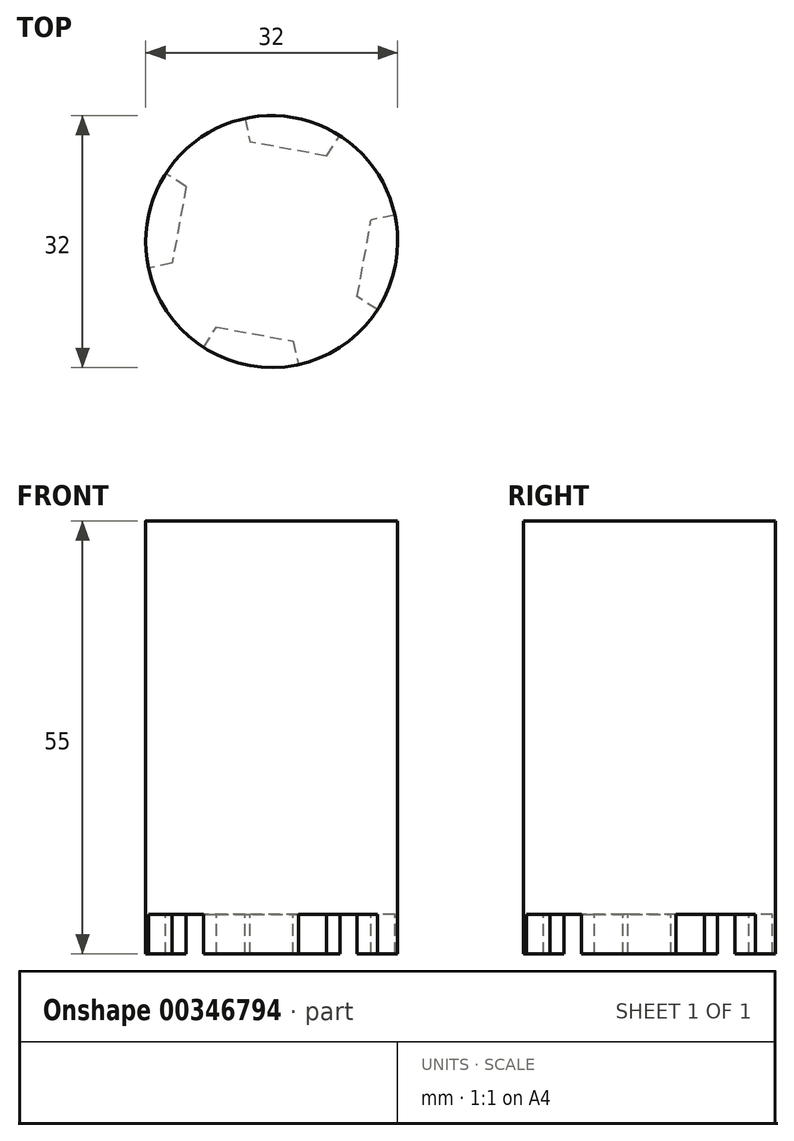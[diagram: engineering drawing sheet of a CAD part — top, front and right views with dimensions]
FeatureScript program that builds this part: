
annotation { "Feature Type Name" : "Feature", "Feature Type Description" : "" }
export const myFeature = defineFeature(function(context is Context, id is Id, definition is map)
    precondition{}
    {
        {
            var Q0;
            Q0=qCreatedBy(makeId("Top.planeOp"),FACE);
            var sketch = newSketch(context, id + "F0", { "sketchPlane" : qUnion([Q0])});
            skCircle(sketch, "E0", {"center": v(41.4, -34.31) * mm, "radius": 16 * mm});
            skSolve(sketch);
        }
        {
            var Q0;
            Q0 = qSketchRegion(id + "F0", true);
            extrude(context, id + "F1", {"entities" : qUnion([Q0]), "depth" : 50 * mm});
        }
        {
            var Q0;
            Q0=makeQuery(id+"F1.opExtrude","CAP_FACE",FACE,{"disambiguationData":[OSD([sQuery(id+"F0.wireOp",EDGE,"E0")])],"isStart":true});
            var sketch = newSketch(context, id + "F2", { "sketchPlane" : qUnion([Q0])});
            skCircle(sketch, "E1.0", {"center": v(41.4, 34.31) * mm, "radius": 16 * mm});
            skCircle(sketch, "E2.cCircle", {"center": v(41.4, 34.31) * mm, "radius": 16 * mm, "construction": true});
            skLineSegment(sketch, "E2.0", {"start": v(57.04, 30.92) * mm, "end": v(50.06, 20.86) * mm});
            skLineSegment(sketch, "E2.1", {"start": v(50.06, 20.86) * mm, "end": v(38.01, 18.68) * mm});
            skLineSegment(sketch, "E2.2", {"start": v(38.01, 18.68) * mm, "end": v(27.95, 25.66) * mm});
            skLineSegment(sketch, "E2.3", {"start": v(27.95, 25.66) * mm, "end": v(25.77, 37.7) * mm});
            skLineSegment(sketch, "E2.4", {"start": v(25.77, 37.7) * mm, "end": v(32.74, 47.77) * mm});
            skLineSegment(sketch, "E2.5", {"start": v(32.74, 47.77) * mm, "end": v(44.8, 49.95) * mm});
            skLineSegment(sketch, "E2.6", {"start": v(44.8, 49.95) * mm, "end": v(54.86, 42.97) * mm});
            skLineSegment(sketch, "E2.7", {"start": v(54.86, 42.97) * mm, "end": v(57.04, 30.92) * mm});
            skLineSegment(sketch, "E3", {"start": v(54.86, 42.97) * mm, "end": v(27.95, 25.66) * mm});
            skLineSegment(sketch, "E4", {"start": v(57.04, 30.92) * mm, "end": v(25.77, 37.7) * mm});
            skLineSegment(sketch, "E5", {"start": v(32.74, 47.77) * mm, "end": v(50.06, 20.86) * mm});
            skLineSegment(sketch, "E6", {"start": v(38.01, 18.68) * mm, "end": v(44.8, 49.95) * mm});
            skCircle(sketch, "E7.cCircle", {"center": v(41.4, 34.31) * mm, "radius": 12.93 * mm, "construction": true});
            skLineSegment(sketch, "E7.0", {"start": v(54.04, 31.57) * mm, "end": v(48.4, 23.44) * mm});
            skLineSegment(sketch, "E7.1", {"start": v(48.4, 23.44) * mm, "end": v(38.66, 21.68) * mm});
            skLineSegment(sketch, "E7.2", {"start": v(38.66, 21.68) * mm, "end": v(30.53, 27.32) * mm});
            skLineSegment(sketch, "E7.3", {"start": v(30.53, 27.32) * mm, "end": v(28.77, 37.05) * mm});
            skLineSegment(sketch, "E7.4", {"start": v(28.77, 37.05) * mm, "end": v(34.4, 45.19) * mm});
            skLineSegment(sketch, "E7.5", {"start": v(34.4, 45.19) * mm, "end": v(44.14, 46.95) * mm});
            skLineSegment(sketch, "E7.6", {"start": v(44.14, 46.95) * mm, "end": v(52.28, 41.31) * mm});
            skLineSegment(sketch, "E7.7", {"start": v(52.28, 41.31) * mm, "end": v(54.04, 31.57) * mm});
            skSolve(sketch);
        }
        {
            var Q0;
            {var subQ0=sQuery(id+"F2.wireOp",EDGE,"E2.7");Q0=makeQuery(id+"F2.imprint","IMPRINT",FACE,{"disambiguationData":[TD([[makeQuery(id+"F2.imprint","IMPRINT",EDGE,{"derivedFrom":subQ0}),-1.0]])]});}
            var Q1;
            {var subQ0=sQuery(id+"F2.wireOp",EDGE,"E2.7");Q1=makeQuery(id+"F2.imprint","IMPRINT",FACE,{"disambiguationData":[TD([[makeQuery(id+"F2.imprint","IMPRINT",EDGE,{"derivedFrom":subQ0}),1.0]])]});}
            var Q2;
            {var subQ0=sQuery(id+"F2.wireOp",EDGE,"E2.1");Q2=makeQuery(id+"F2.imprint","IMPRINT",FACE,{"disambiguationData":[TD([[makeQuery(id+"F2.imprint","IMPRINT",EDGE,{"derivedFrom":subQ0}),-1.0]])]});}
            var Q3;
            {var subQ0=sQuery(id+"F2.wireOp",EDGE,"E2.1");Q3=makeQuery(id+"F2.imprint","IMPRINT",FACE,{"disambiguationData":[TD([[makeQuery(id+"F2.imprint","IMPRINT",EDGE,{"derivedFrom":subQ0}),1.0]])]});}
            var Q4;
            {var subQ0=sQuery(id+"F2.wireOp",EDGE,"E2.3");Q4=makeQuery(id+"F2.imprint","IMPRINT",FACE,{"disambiguationData":[TD([[makeQuery(id+"F2.imprint","IMPRINT",EDGE,{"derivedFrom":subQ0}),-1.0]])]});}
            var Q5;
            {var subQ0=sQuery(id+"F2.wireOp",EDGE,"E2.3");Q5=makeQuery(id+"F2.imprint","IMPRINT",FACE,{"disambiguationData":[TD([[makeQuery(id+"F2.imprint","IMPRINT",EDGE,{"derivedFrom":subQ0}),1.0]])]});}
            var Q6;
            {var subQ0=sQuery(id+"F2.wireOp",EDGE,"E2.5");Q6=makeQuery(id+"F2.imprint","IMPRINT",FACE,{"disambiguationData":[TD([[makeQuery(id+"F2.imprint","IMPRINT",EDGE,{"derivedFrom":subQ0}),-1.0]])]});}
            var Q7;
            {var subQ0=sQuery(id+"F2.wireOp",EDGE,"E2.5");Q7=makeQuery(id+"F2.imprint","IMPRINT",FACE,{"disambiguationData":[TD([[makeQuery(id+"F2.imprint","IMPRINT",EDGE,{"derivedFrom":subQ0}),1.0]])]});}
            extrude(context, id + "F3", {"entities" : qUnion([Q0, Q1, Q2, Q3, Q4, Q5, Q6, Q7]), "operationType" : NewBodyOperationType.ADD, "depth" : 5 * mm});
        }
    });
